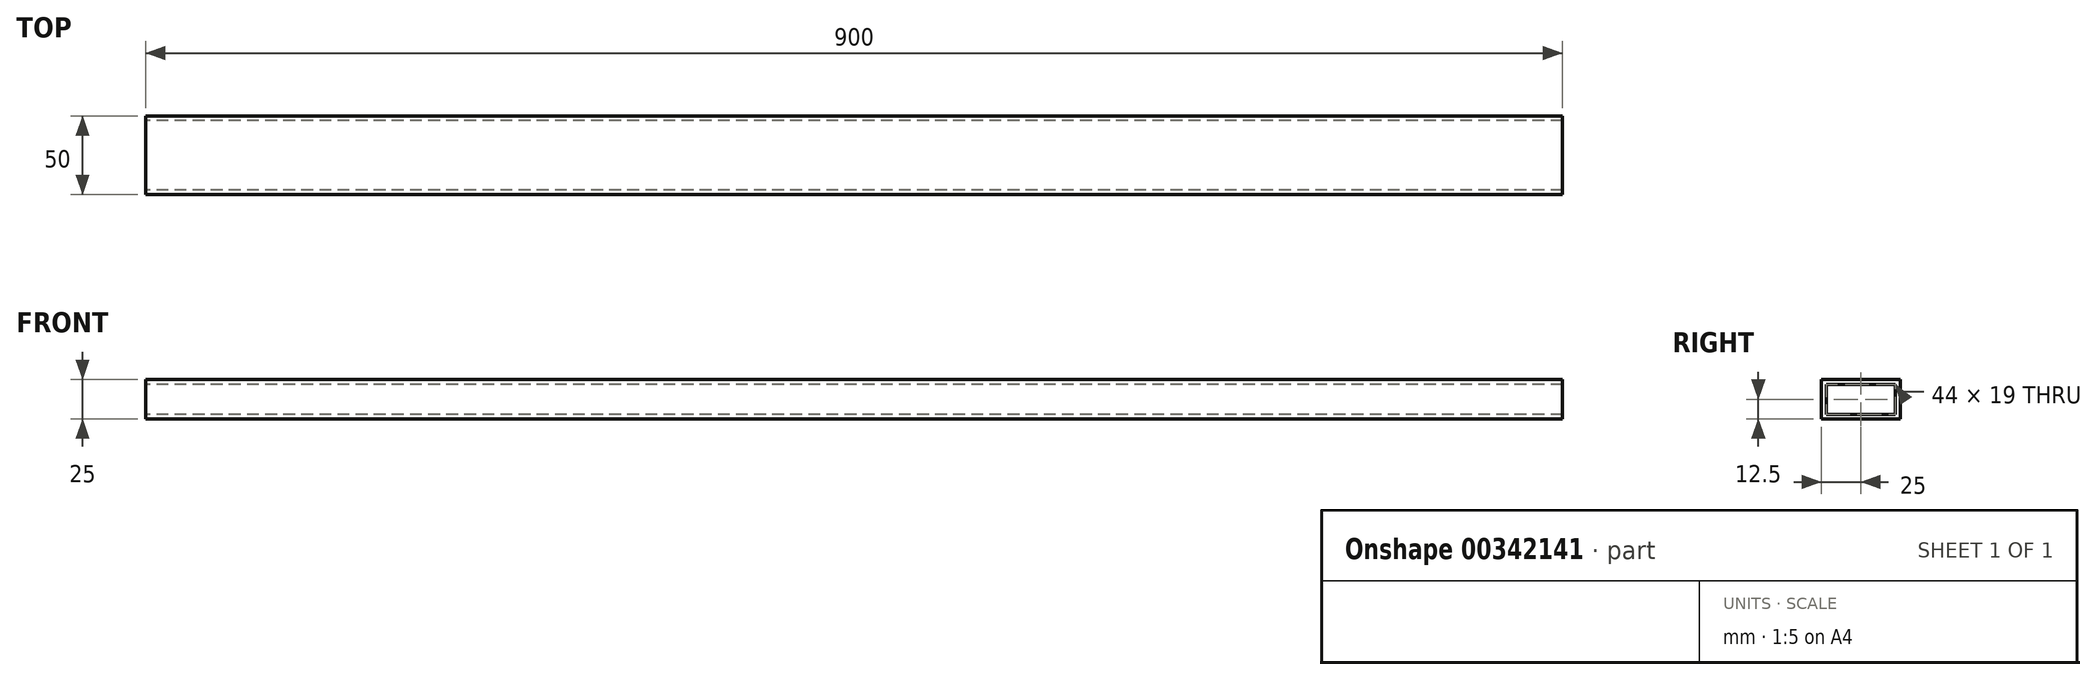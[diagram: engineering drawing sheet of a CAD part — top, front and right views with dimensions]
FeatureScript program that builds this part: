
annotation { "Feature Type Name" : "Feature", "Feature Type Description" : "" }
export const myFeature = defineFeature(function(context is Context, id is Id, definition is map)
    precondition{}
    {
        {
            var Q0;
            Q0=qCreatedBy(makeId("Right.planeOp"),FACE);
            var sketch = newSketch(context, id + "F0", { "sketchPlane" : qUnion([Q0])});
            skLineSegment(sketch, "E0.bottom", {"start": v(-25, 12.5) * mm, "end": v(25, 12.5) * mm});
            skLineSegment(sketch, "E0.top", {"start": v(-25, -12.5) * mm, "end": v(25, -12.5) * mm});
            skLineSegment(sketch, "E0.left", {"start": v(-25, 12.5) * mm, "end": v(-25, -12.5) * mm});
            skLineSegment(sketch, "E0.right", {"start": v(25, 12.5) * mm, "end": v(25, -12.5) * mm});
            skPoint(sketch, "E0.middle", {"position": v(0, 0) * mm});
            skLineSegment(sketch, "E1.bottom", {"start": v(-22, 9.5) * mm, "end": v(22, 9.5) * mm});
            skLineSegment(sketch, "E1.top", {"start": v(-22, -9.5) * mm, "end": v(22, -9.5) * mm});
            skLineSegment(sketch, "E1.left", {"start": v(-22, 9.5) * mm, "end": v(-22, -9.5) * mm});
            skLineSegment(sketch, "E1.right", {"start": v(22, 9.5) * mm, "end": v(22, -9.5) * mm});
            skSolve(sketch);
        }
        {
            var Q0;
            Q0=qSketchRegion(id+"F0",true);
            extrude(context, id + "F1", {"entities" : qUnion([Q0]), "endBound" : BoundingType.SYMMETRIC, "depth" : 900 * mm});
        }
    });
